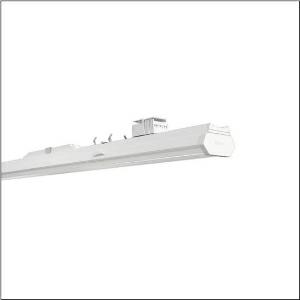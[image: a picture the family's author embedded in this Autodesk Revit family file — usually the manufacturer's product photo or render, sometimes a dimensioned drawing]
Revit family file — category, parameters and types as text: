
# Revit family: licross_11_protected_mo_51tp12dn495g3c
name_source: partatom
category: Lighting Fixtures
units: mm (PartAtom-declared; Revit-internal decimal feet)

## family parameters
Cut with Voids When Loaded = No
Host = Face
Light Source = No
Part Type = Normal
Room Calculation Point = No
Round Connector Dimension = Use Diameter
Shared = No

## types (1)
- --- (1 x LED, 980 lm, 6.8 W, 4000K)
    Apparent Load = 7 VA
    CIE Flux Codes = 73 92 98 99 100
    Color Rendering = 80
    Color Temperature = 4000K
    Default Elevation = 1800 mm
    Description = Licross 11 Protected MO, luminaire insert, of sheet steel, galvanised, coil coated, white, length: 1.500mm, width: 90mm, height: 101mm, LED rated luminous flux: 9.980lm, light colour: 840, SDCM (Standard Deviation of Colour Matching)MacAdam ≤ 2 SDCM (initial), control gear: DALI 2 (for two DALI lines), with plug, 6-pole, with phase selection, for trunking rail, 14-core, mains connection: 220..240V, AC, 50/60Hz, rated input power: 61W, for trunking rail, 14-core, internal wiring halogen-free, for emergency light function, converter,control gear: single battery element, battery: LiFePO4, 9Ah, primary light control with lens, of plastic, primary optical cover: cover, of PMMA, light emission: direct distribution, primary light characteristic: symmetric, protection rating (complete): IP64, insulation class (complete): insulation class I (protective earthing), certification: CE, UKCA, protection symbol: D if used in an environment with conductive dust loads with corresponding accessories, impact resistance: IK06, permissible ambient temperature for indoor applications: +5..+35°C, standard: EN 60598-2-22, LABS conformity tested according to VDMA 24364:2018-05, reducing of maximum allowable ambient temperature of 5°C with ceiling mounting, corresponds to IFS (International Featured Standards) requirements for safety and quality in the food industry, The light source and the operating device comply with the requirements of the Ecodesign Regulation (EU) 2019/2020 and are replaceable in accordance with this regulation, packaging unit: 1 piece
    Height = 92 mm
    Lamp = 1 x LED
    Lamp Light Flux = 980 lm
    Lamp Power = 6.8 W
    Lamp count = 1
    Length = 1500 mm
    Luminous efficacy = 144 lm/W
    Manufacturer = Siteco
    ModVariant = No
    Model = 51TP12DN495G3C
    Mounting Place = Ceiling
    Mounting Type = Pendant
    Number of Poles = 1
    OnlyDefault = Yes
    Power Factor = 1
    Product Name = Licross 11 Protected MO
    Product group = luminaire insert | ceiling pendant
    ProductGroupID = 901
    Protection Class = Protection class I
    Protection Degree = IP 64
    RLX_Detail_Level = 1
    RLX_Emergency_Light_Flux = 0 lm
    RLX_Emergency_Type = 0
    RLX_Emergency_Type_DB = No
    RlxData = <blob elided: 25033 chars, md5=63ea8ea9>
    Socket = socket
    Standby Power = 0 W
    System Light Flux = 980 lm
    System Power = 7 W
    Type Comments = : emergency light operation: 3 h
    Type Image = l_1256148.jpg
    URL = http://relux.com
    VarID = @adj_094523
    Voltage = 0 V
    Weight = 0.00 kg
    Width = 88 mm

## geometry (parser evidence)
native form markers: Blend x4, Sweep x10
no freeform markers — native parametric forms only
